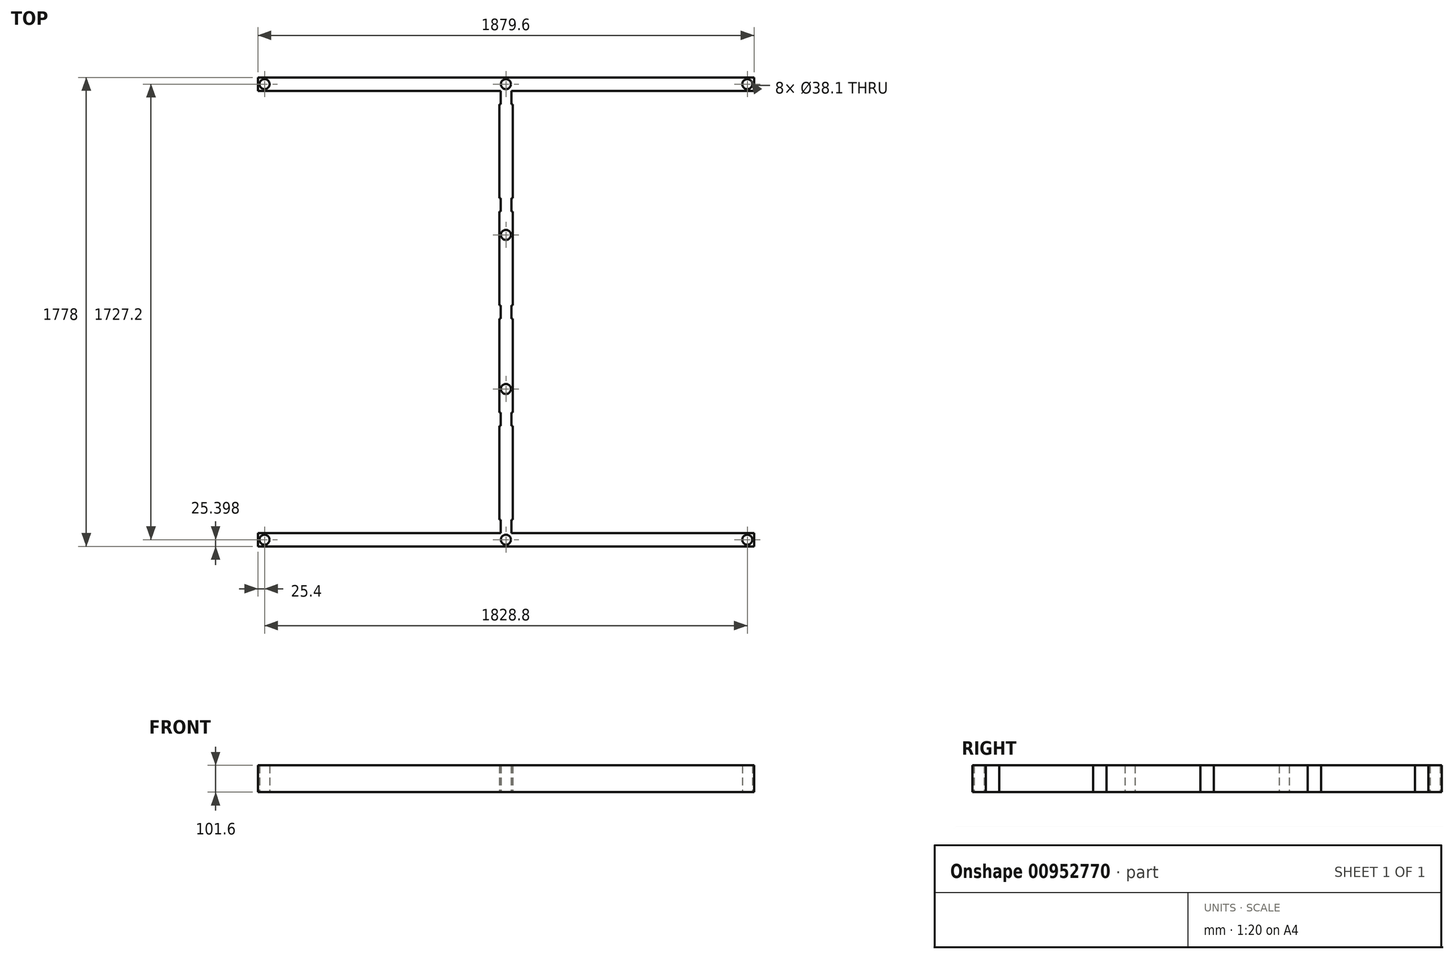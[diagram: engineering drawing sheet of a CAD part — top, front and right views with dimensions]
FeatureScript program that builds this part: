
annotation { "Feature Type Name" : "Feature", "Feature Type Description" : "" }
export const myFeature = defineFeature(function(context is Context, id is Id, definition is map)
    precondition{}
    {
        {
            var Q0;
            Q0=qCreatedBy(makeId("Top.planeOp"),FACE);
            var sketch = newSketch(context, id + "F0", { "sketchPlane" : qUnion([Q0])});
            skLineSegment(sketch, "E0", {"start": v(-50.8, 1680.24) * mm, "end": v(-50.8, 3.84) * mm});
            skLineSegment(sketch, "E1", {"start": v(0, 3.84) * mm, "end": v(0, 1680.24) * mm});
            skLineSegment(sketch, "E2", {"start": v(-50.8, 1731.04) * mm, "end": v(0, 1731.04) * mm});
            skLineSegment(sketch, "E3", {"start": v(-50.8, 1731.04) * mm, "end": v(-965.2, 1731.04) * mm});
            skLineSegment(sketch, "E4", {"start": v(-965.2, 1731.04) * mm, "end": v(-965.2, 1680.24) * mm});
            skLineSegment(sketch, "E5", {"start": v(-965.2, 1680.24) * mm, "end": v(-50.8, 1680.24) * mm});
            skLineSegment(sketch, "E6", {"start": v(0, 1680.24) * mm, "end": v(914.4, 1680.24) * mm});
            skLineSegment(sketch, "E7", {"start": v(914.4, 1680.24) * mm, "end": v(914.4, 1731.04) * mm});
            skLineSegment(sketch, "E8", {"start": v(914.4, 1731.04) * mm, "end": v(0, 1731.04) * mm});
            skLineSegment(sketch, "E9", {"start": v(-50.8, -46.96) * mm, "end": v(0, -46.96) * mm});
            skLineSegment(sketch, "E10", {"start": v(0, 3.84) * mm, "end": v(914.4, 3.84) * mm});
            skLineSegment(sketch, "E11", {"start": v(914.4, 3.84) * mm, "end": v(914.4, -46.96) * mm});
            skLineSegment(sketch, "E12", {"start": v(914.4, -46.96) * mm, "end": v(0, -46.96) * mm});
            skLineSegment(sketch, "E13", {"start": v(-50.8, -46.96) * mm, "end": v(-965.2, -46.96) * mm});
            skLineSegment(sketch, "E14", {"start": v(-965.2, -46.96) * mm, "end": v(-965.2, 3.84) * mm});
            skLineSegment(sketch, "E15", {"start": v(-965.2, 3.84) * mm, "end": v(-50.8, 3.84) * mm});
            skLineSegment(sketch, "E16", {"start": v(-50.8, 1680.24) * mm, "end": v(-50.8, 1629.44) * mm});
            skLineSegment(sketch, "E17", {"start": v(-50.8, 1629.44) * mm, "end": v(-50.8, 1273.84) * mm});
            skLineSegment(sketch, "E18", {"start": v(-50.8, 1273.84) * mm, "end": v(-50.8, 1223.04) * mm});
            skLineSegment(sketch, "E19", {"start": v(-50.8, 1223.04) * mm, "end": v(-50.8, 867.44) * mm});
            skLineSegment(sketch, "E20", {"start": v(-50.8, 867.44) * mm, "end": v(-50.8, 816.64) * mm});
            skLineSegment(sketch, "E21", {"start": v(-50.8, 816.64) * mm, "end": v(-50.8, 461.04) * mm});
            skLineSegment(sketch, "E22", {"start": v(-50.8, 461.04) * mm, "end": v(-50.8, 410.24) * mm});
            skLineSegment(sketch, "E23", {"start": v(-50.8, 410.24) * mm, "end": v(-50.8, 54.64) * mm});
            skLineSegment(sketch, "E24", {"start": v(-50.8, 54.64) * mm, "end": v(-50.8, 3.84) * mm});
            skLineSegment(sketch, "E25", {"start": v(-50.8, 54.64) * mm, "end": v(-48.26, 54.64) * mm});
            skLineSegment(sketch, "E26", {"start": v(-48.26, 54.64) * mm, "end": v(-48.26, 60.99) * mm});
            skLineSegment(sketch, "E27", {"start": v(-48.26, 60.99) * mm, "end": v(-45.72, 60.99) * mm});
            skLineSegment(sketch, "E28", {"start": v(-45.72, 60.99) * mm, "end": v(-45.72, -2.51) * mm});
            skLineSegment(sketch, "E29", {"start": v(-45.72, -2.51) * mm, "end": v(-48.26, -2.51) * mm});
            skLineSegment(sketch, "E30", {"start": v(-48.26, -2.51) * mm, "end": v(-48.26, 3.84) * mm});
            skLineSegment(sketch, "E31", {"start": v(-48.26, 3.84) * mm, "end": v(-50.8, 3.84) * mm});
            skLineSegment(sketch, "E32", {"start": v(-50.8, 461.04) * mm, "end": v(-48.26, 461.04) * mm});
            skLineSegment(sketch, "E33", {"start": v(-48.26, 461.04) * mm, "end": v(-48.26, 467.39) * mm});
            skLineSegment(sketch, "E34", {"start": v(-48.26, 467.39) * mm, "end": v(-45.72, 467.39) * mm});
            skLineSegment(sketch, "E35", {"start": v(-45.72, 467.39) * mm, "end": v(-45.72, 403.89) * mm});
            skLineSegment(sketch, "E36", {"start": v(-45.72, 403.89) * mm, "end": v(-48.26, 403.89) * mm});
            skLineSegment(sketch, "E37", {"start": v(-48.26, 403.89) * mm, "end": v(-48.26, 410.24) * mm});
            skLineSegment(sketch, "E38", {"start": v(-48.26, 410.24) * mm, "end": v(-50.8, 410.24) * mm});
            skLineSegment(sketch, "E39", {"start": v(-50.8, 867.44) * mm, "end": v(-48.26, 867.44) * mm});
            skLineSegment(sketch, "E40", {"start": v(-48.26, 867.44) * mm, "end": v(-48.26, 873.79) * mm});
            skLineSegment(sketch, "E41", {"start": v(-48.26, 873.79) * mm, "end": v(-45.72, 873.79) * mm});
            skLineSegment(sketch, "E42", {"start": v(-45.72, 873.79) * mm, "end": v(-45.72, 810.29) * mm});
            skLineSegment(sketch, "E43", {"start": v(-45.72, 810.29) * mm, "end": v(-48.26, 810.29) * mm});
            skLineSegment(sketch, "E44", {"start": v(-48.26, 810.29) * mm, "end": v(-48.26, 816.64) * mm});
            skLineSegment(sketch, "E45", {"start": v(-48.26, 816.64) * mm, "end": v(-50.8, 816.64) * mm});
            skLineSegment(sketch, "E46", {"start": v(-50.8, 1273.84) * mm, "end": v(-48.26, 1273.84) * mm});
            skLineSegment(sketch, "E47", {"start": v(-48.26, 1273.84) * mm, "end": v(-48.26, 1280.19) * mm});
            skLineSegment(sketch, "E48", {"start": v(-48.26, 1280.19) * mm, "end": v(-45.72, 1280.19) * mm});
            skLineSegment(sketch, "E49", {"start": v(-45.72, 1280.19) * mm, "end": v(-45.72, 1216.69) * mm});
            skLineSegment(sketch, "E50", {"start": v(-45.72, 1216.69) * mm, "end": v(-48.26, 1216.69) * mm});
            skLineSegment(sketch, "E51", {"start": v(-48.26, 1216.69) * mm, "end": v(-48.26, 1223.04) * mm});
            skLineSegment(sketch, "E52", {"start": v(-48.26, 1223.04) * mm, "end": v(-50.8, 1223.04) * mm});
            skLineSegment(sketch, "E53", {"start": v(-50.8, 1629.44) * mm, "end": v(-48.26, 1629.44) * mm});
            skLineSegment(sketch, "E54", {"start": v(-48.26, 1629.44) * mm, "end": v(-48.26, 1623.09) * mm});
            skLineSegment(sketch, "E55", {"start": v(-48.26, 1623.09) * mm, "end": v(-45.72, 1623.09) * mm});
            skLineSegment(sketch, "E56", {"start": v(-45.72, 1623.09) * mm, "end": v(-45.72, 1686.59) * mm});
            skLineSegment(sketch, "E57", {"start": v(-45.72, 1686.59) * mm, "end": v(-48.26, 1686.59) * mm});
            skLineSegment(sketch, "E58", {"start": v(-48.26, 1686.59) * mm, "end": v(-48.26, 1680.24) * mm});
            skLineSegment(sketch, "E59", {"start": v(-48.26, 1680.24) * mm, "end": v(-50.8, 1680.24) * mm});
            skLineSegment(sketch, "E60", {"start": v(-50.8, 1731.04) * mm, "end": v(-25.4, 1731.04) * mm});
            skLineSegment(sketch, "E61", {"start": v(-965.2, 3.84) * mm, "end": v(-939.8, 3.84) * mm});
            skPoint(sketch, "E62.centerSnap0", {"position": v(-50.8, 638.84) * mm});
            skLineSegment(sketch, "E63", {"start": v(0, 3.84) * mm, "end": v(-2.54, 3.84) * mm});
            skLineSegment(sketch, "E64", {"start": v(-2.54, 3.84) * mm, "end": v(-2.54, -2.51) * mm});
            skLineSegment(sketch, "E65", {"start": v(-2.54, -2.51) * mm, "end": v(-5.08, -2.51) * mm});
            skLineSegment(sketch, "E66", {"start": v(-5.08, -2.51) * mm, "end": v(-5.08, 60.99) * mm});
            skLineSegment(sketch, "E67", {"start": v(-5.08, 60.99) * mm, "end": v(-2.54, 60.99) * mm});
            skLineSegment(sketch, "E68", {"start": v(-2.54, 60.99) * mm, "end": v(-2.54, 54.64) * mm});
            skLineSegment(sketch, "E69", {"start": v(-2.54, 54.64) * mm, "end": v(0, 54.64) * mm});
            skLineSegment(sketch, "E70", {"start": v(0, 461.04) * mm, "end": v(-2.54, 461.04) * mm});
            skLineSegment(sketch, "E71", {"start": v(-2.54, 461.04) * mm, "end": v(-2.54, 467.39) * mm});
            skLineSegment(sketch, "E72", {"start": v(-2.54, 467.39) * mm, "end": v(-5.08, 467.39) * mm});
            skLineSegment(sketch, "E73", {"start": v(-5.08, 467.39) * mm, "end": v(-5.08, 403.89) * mm});
            skLineSegment(sketch, "E74", {"start": v(-5.08, 403.89) * mm, "end": v(-2.54, 403.89) * mm});
            skLineSegment(sketch, "E75", {"start": v(-2.54, 403.89) * mm, "end": v(-2.54, 410.24) * mm});
            skLineSegment(sketch, "E76", {"start": v(-2.54, 410.24) * mm, "end": v(0, 410.24) * mm});
            skLineSegment(sketch, "E77", {"start": v(0, 867.44) * mm, "end": v(-2.54, 867.44) * mm});
            skLineSegment(sketch, "E78", {"start": v(-2.54, 867.44) * mm, "end": v(-2.54, 873.79) * mm});
            skLineSegment(sketch, "E79", {"start": v(-2.54, 873.79) * mm, "end": v(-5.08, 873.79) * mm});
            skLineSegment(sketch, "E80", {"start": v(-5.08, 873.79) * mm, "end": v(-5.08, 810.29) * mm});
            skLineSegment(sketch, "E81", {"start": v(-5.08, 810.29) * mm, "end": v(-2.54, 810.29) * mm});
            skLineSegment(sketch, "E82", {"start": v(-2.54, 810.29) * mm, "end": v(-2.54, 816.64) * mm});
            skLineSegment(sketch, "E83", {"start": v(-2.54, 816.64) * mm, "end": v(0, 816.64) * mm});
            skLineSegment(sketch, "E84", {"start": v(0, 1273.84) * mm, "end": v(-2.54, 1273.84) * mm});
            skLineSegment(sketch, "E85", {"start": v(-2.54, 1273.84) * mm, "end": v(-2.54, 1280.19) * mm});
            skLineSegment(sketch, "E86", {"start": v(-2.54, 1280.19) * mm, "end": v(-5.08, 1280.19) * mm});
            skLineSegment(sketch, "E87", {"start": v(-5.08, 1280.19) * mm, "end": v(-5.08, 1216.69) * mm});
            skLineSegment(sketch, "E88", {"start": v(-5.08, 1216.69) * mm, "end": v(-2.54, 1216.69) * mm});
            skLineSegment(sketch, "E89", {"start": v(-2.54, 1216.69) * mm, "end": v(-2.54, 1223.04) * mm});
            skLineSegment(sketch, "E90", {"start": v(-2.54, 1223.04) * mm, "end": v(0, 1223.04) * mm});
            skLineSegment(sketch, "E91", {"start": v(0, 1680.24) * mm, "end": v(-2.54, 1680.24) * mm});
            skLineSegment(sketch, "E92", {"start": v(-2.54, 1680.24) * mm, "end": v(-2.54, 1686.59) * mm});
            skLineSegment(sketch, "E93", {"start": v(-2.54, 1686.59) * mm, "end": v(-5.08, 1686.59) * mm});
            skLineSegment(sketch, "E94", {"start": v(-5.08, 1686.59) * mm, "end": v(-5.08, 1623.09) * mm});
            skLineSegment(sketch, "E95", {"start": v(-5.08, 1623.09) * mm, "end": v(-2.54, 1623.09) * mm});
            skLineSegment(sketch, "E96", {"start": v(-2.54, 1623.09) * mm, "end": v(-2.54, 1629.44) * mm});
            skLineSegment(sketch, "E97", {"start": v(-2.54, 1629.44) * mm, "end": v(0, 1629.44) * mm});
            skCircle(sketch, "E98", {"center": v(-939.8, -21.56) * mm, "radius": 19.05 * mm});
            skCircle(sketch, "E99", {"center": v(889, 1705.64) * mm, "radius": 19.05 * mm});
            skCircle(sketch, "E100", {"center": v(-25.4, 1705.64) * mm, "radius": 19.05 * mm});
            skCircle(sketch, "E101", {"center": v(-939.55, 1705.64) * mm, "radius": 19.05 * mm});
            skCircle(sketch, "E102", {"center": v(-25.4, -21.56) * mm, "radius": 19.05 * mm});
            skCircle(sketch, "E103", {"center": v(889, -21.56) * mm, "radius": 19.05 * mm});
            skLineSegment(sketch, "E104", {"start": v(-50.8, 461.04) * mm, "end": v(-50.8, 549.94) * mm});
            skLineSegment(sketch, "E105", {"start": v(-50.8, 1223.04) * mm, "end": v(-50.8, 1134.14) * mm});
            skCircle(sketch, "E106", {"center": v(-25.4, 1134.14) * mm, "radius": 19.05 * mm});
            skCircle(sketch, "E107", {"center": v(-25.4, 549.94) * mm, "radius": 19.05 * mm});
            skLineSegment(sketch, "E108", {"start": v(-48.26, 54.64) * mm, "end": v(-45.72, 54.64) * mm});
            skLineSegment(sketch, "E109", {"start": v(-48.26, 3.84) * mm, "end": v(-45.72, 3.84) * mm});
            skLineSegment(sketch, "E110", {"start": v(-2.54, 54.64) * mm, "end": v(-5.08, 54.64) * mm});
            skLineSegment(sketch, "E111", {"start": v(-2.54, 3.84) * mm, "end": v(-5.08, 3.84) * mm});
            skLineSegment(sketch, "E112", {"start": v(-48.26, 461.04) * mm, "end": v(-45.72, 461.04) * mm});
            skLineSegment(sketch, "E113", {"start": v(-48.26, 410.24) * mm, "end": v(-45.72, 410.24) * mm});
            skLineSegment(sketch, "E114", {"start": v(-2.54, 410.24) * mm, "end": v(-5.08, 410.24) * mm});
            skLineSegment(sketch, "E115", {"start": v(-2.54, 461.04) * mm, "end": v(-5.08, 461.04) * mm});
            skLineSegment(sketch, "E116", {"start": v(-48.26, 867.44) * mm, "end": v(-45.72, 867.44) * mm});
            skLineSegment(sketch, "E117", {"start": v(-48.26, 816.64) * mm, "end": v(-45.72, 816.64) * mm});
            skLineSegment(sketch, "E118", {"start": v(-2.54, 867.44) * mm, "end": v(-5.08, 867.44) * mm});
            skLineSegment(sketch, "E119", {"start": v(-2.54, 816.64) * mm, "end": v(-5.08, 816.64) * mm});
            skLineSegment(sketch, "E120", {"start": v(-48.26, 1273.84) * mm, "end": v(-45.72, 1273.84) * mm});
            skLineSegment(sketch, "E121", {"start": v(-48.26, 1223.04) * mm, "end": v(-45.72, 1223.04) * mm});
            skLineSegment(sketch, "E122", {"start": v(-2.54, 1273.84) * mm, "end": v(-5.08, 1273.84) * mm});
            skLineSegment(sketch, "E123", {"start": v(-2.54, 1223.04) * mm, "end": v(-5.08, 1223.04) * mm});
            skLineSegment(sketch, "E124", {"start": v(-48.26, 1680.24) * mm, "end": v(-45.72, 1680.24) * mm});
            skLineSegment(sketch, "E125", {"start": v(-48.26, 1629.44) * mm, "end": v(-45.72, 1629.44) * mm});
            skLineSegment(sketch, "E126", {"start": v(-2.54, 1629.44) * mm, "end": v(-5.08, 1629.44) * mm});
            skLineSegment(sketch, "E127", {"start": v(-2.54, 1680.24) * mm, "end": v(-5.08, 1680.24) * mm});
            skSolve(sketch);
        }
        {
            var Q0;
            Q0=makeQuery(id+"F0.imprint","IMPRINT",FACE,{"disambiguationData":[TD([[makeQuery(id+"F0.imprint","IMPRINT",EDGE,{"derivedFrom":sQuery(id+"F0.wireOp",EDGE,"E2")}),-1.0]])]});
            var Q1;
            {var subQ0=sQuery(id+"F0.wireOp",EDGE,"E29");Q1=makeQuery(id+"F0.imprint","IMPRINT",FACE,{"disambiguationData":[TD([[makeQuery(id+"F0.imprint","IMPRINT",EDGE,{"derivedFrom":subQ0}),-1.0]])]});}
            var Q2;
            Q2=makeQuery(id+"F0.imprint","IMPRINT",FACE,{"disambiguationData":[TD([[makeQuery(id+"F0.imprint","IMPRINT",EDGE,{"derivedFrom":sQuery(id+"F0.wireOp",EDGE,"E64")}),-1.0]])]});
            var Q3;
            {var subQ0=sQuery(id+"F0.wireOp",EDGE,"E67");Q3=makeQuery(id+"F0.imprint","IMPRINT",FACE,{"disambiguationData":[TD([[makeQuery(id+"F0.imprint","IMPRINT",EDGE,{"derivedFrom":subQ0}),-1.0]])]});}
            var Q4;
            Q4=makeQuery(id+"F0.imprint","IMPRINT",FACE,{"disambiguationData":[TD([[makeQuery(id+"F0.imprint","IMPRINT",EDGE,{"derivedFrom":sQuery(id+"F0.wireOp",EDGE,"E26")}),-1.0]])]});
            var Q5;
            Q5=makeQuery(id+"F0.imprint","IMPRINT",FACE,{"disambiguationData":[TD([[makeQuery(id+"F0.imprint","IMPRINT",EDGE,{"derivedFrom":sQuery(id+"F0.wireOp",EDGE,"E33")}),-1.0]])]});
            var Q6;
            {var subQ0=sQuery(id+"F0.wireOp",EDGE,"E36");Q6=makeQuery(id+"F0.imprint","IMPRINT",FACE,{"disambiguationData":[TD([[makeQuery(id+"F0.imprint","IMPRINT",EDGE,{"derivedFrom":subQ0}),-1.0]])]});}
            var Q7;
            {var subQ0=sQuery(id+"F0.wireOp",EDGE,"E74");Q7=makeQuery(id+"F0.imprint","IMPRINT",FACE,{"disambiguationData":[TD([[makeQuery(id+"F0.imprint","IMPRINT",EDGE,{"derivedFrom":subQ0}),1.0]])]});}
            var Q8;
            Q8=makeQuery(id+"F0.imprint","IMPRINT",FACE,{"disambiguationData":[TD([[makeQuery(id+"F0.imprint","IMPRINT",EDGE,{"derivedFrom":sQuery(id+"F0.wireOp",EDGE,"E71")}),1.0]])]});
            var Q9;
            Q9=makeQuery(id+"F0.imprint","IMPRINT",FACE,{"disambiguationData":[TD([[makeQuery(id+"F0.imprint","IMPRINT",EDGE,{"derivedFrom":sQuery(id+"F0.wireOp",EDGE,"E40")}),-1.0]])]});
            var Q10;
            Q10=makeQuery(id+"F0.imprint","IMPRINT",FACE,{"disambiguationData":[TD([[makeQuery(id+"F0.imprint","IMPRINT",EDGE,{"derivedFrom":sQuery(id+"F0.wireOp",EDGE,"E78")}),1.0]])]});
            var Q11;
            {var subQ0=sQuery(id+"F0.wireOp",EDGE,"E81");Q11=makeQuery(id+"F0.imprint","IMPRINT",FACE,{"disambiguationData":[TD([[makeQuery(id+"F0.imprint","IMPRINT",EDGE,{"derivedFrom":subQ0}),1.0]])]});}
            var Q12;
            {var subQ0=sQuery(id+"F0.wireOp",EDGE,"E43");Q12=makeQuery(id+"F0.imprint","IMPRINT",FACE,{"disambiguationData":[TD([[makeQuery(id+"F0.imprint","IMPRINT",EDGE,{"derivedFrom":subQ0}),-1.0]])]});}
            var Q13;
            Q13=makeQuery(id+"F0.imprint","IMPRINT",FACE,{"disambiguationData":[TD([[makeQuery(id+"F0.imprint","IMPRINT",EDGE,{"derivedFrom":sQuery(id+"F0.wireOp",EDGE,"E47")}),-1.0]])]});
            var Q14;
            Q14=makeQuery(id+"F0.imprint","IMPRINT",FACE,{"disambiguationData":[TD([[makeQuery(id+"F0.imprint","IMPRINT",EDGE,{"derivedFrom":sQuery(id+"F0.wireOp",EDGE,"E85")}),1.0]])]});
            var Q15;
            {var subQ0=sQuery(id+"F0.wireOp",EDGE,"E88");Q15=makeQuery(id+"F0.imprint","IMPRINT",FACE,{"disambiguationData":[TD([[makeQuery(id+"F0.imprint","IMPRINT",EDGE,{"derivedFrom":subQ0}),1.0]])]});}
            var Q16;
            {var subQ0=sQuery(id+"F0.wireOp",EDGE,"E50");Q16=makeQuery(id+"F0.imprint","IMPRINT",FACE,{"disambiguationData":[TD([[makeQuery(id+"F0.imprint","IMPRINT",EDGE,{"derivedFrom":subQ0}),-1.0]])]});}
            var Q17;
            {var subQ0=sQuery(id+"F0.wireOp",EDGE,"E57");Q17=makeQuery(id+"F0.imprint","IMPRINT",FACE,{"disambiguationData":[TD([[makeQuery(id+"F0.imprint","IMPRINT",EDGE,{"derivedFrom":subQ0}),1.0]])]});}
            var Q18;
            Q18=makeQuery(id+"F0.imprint","IMPRINT",FACE,{"disambiguationData":[TD([[makeQuery(id+"F0.imprint","IMPRINT",EDGE,{"derivedFrom":sQuery(id+"F0.wireOp",EDGE,"E92")}),1.0]])]});
            var Q19;
            {var subQ0=sQuery(id+"F0.wireOp",EDGE,"E95");Q19=makeQuery(id+"F0.imprint","IMPRINT",FACE,{"disambiguationData":[TD([[makeQuery(id+"F0.imprint","IMPRINT",EDGE,{"derivedFrom":subQ0}),1.0]])]});}
            var Q20;
            Q20=makeQuery(id+"F0.imprint","IMPRINT",FACE,{"disambiguationData":[TD([[makeQuery(id+"F0.imprint","IMPRINT",EDGE,{"derivedFrom":sQuery(id+"F0.wireOp",EDGE,"E54")}),1.0]])]});
            extrude(context, id + "F1", {"entities" : qUnion([Q0, Q1, Q2, Q3, Q4, Q5, Q6, Q7, Q8, Q9, Q10, Q11, Q12, Q13, Q14, Q15, Q16, Q17, Q18, Q19, Q20]), "depth" : 101.6 * mm, "offsetDistance" : 25.4 * mm});
        }
    });
